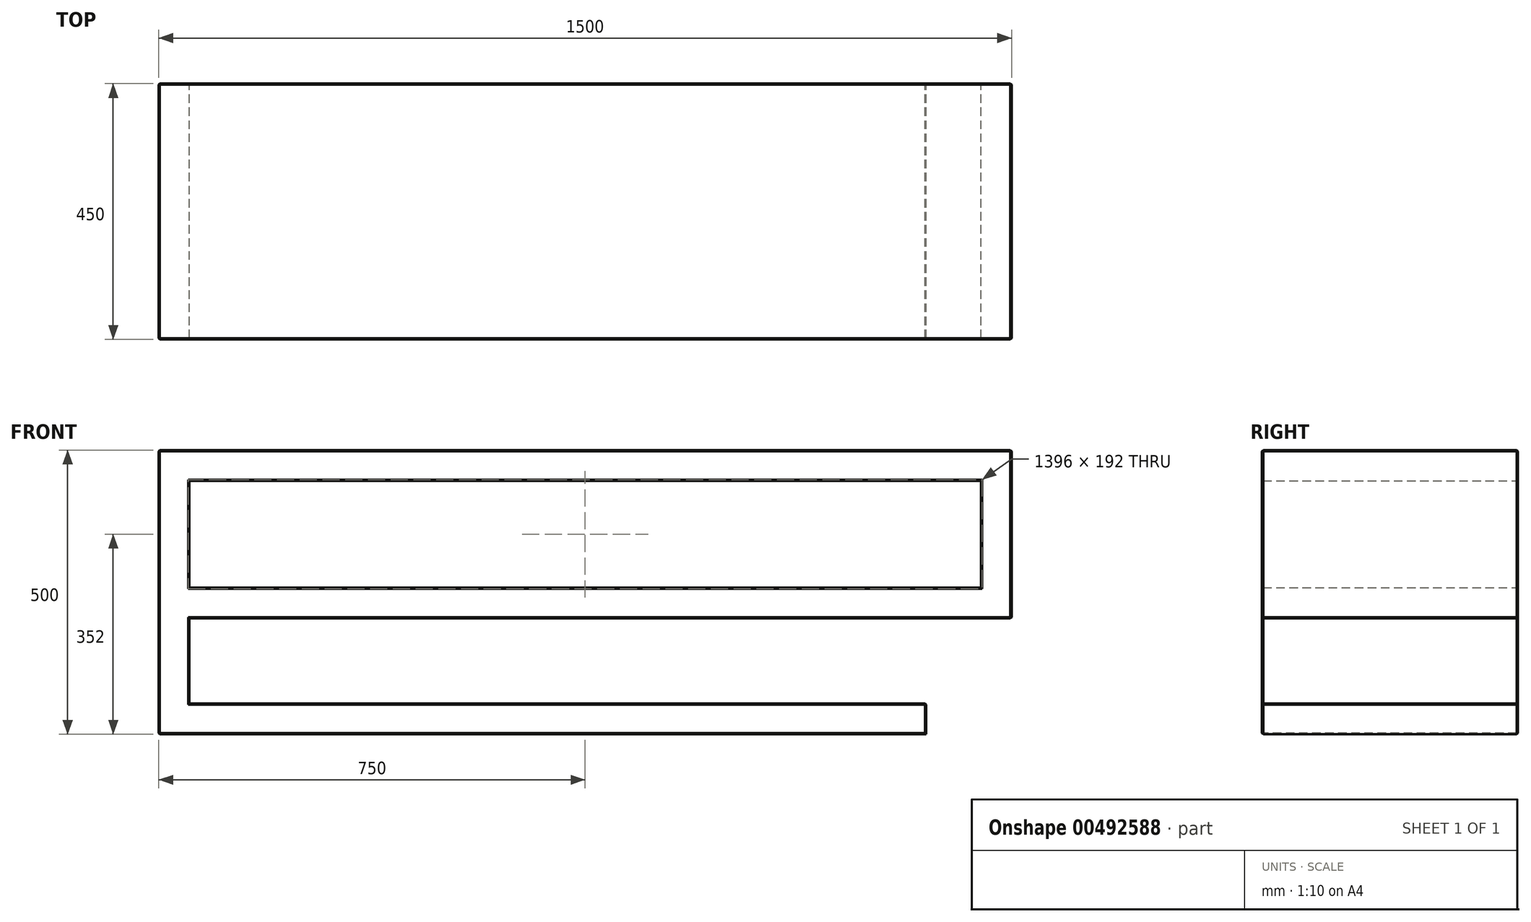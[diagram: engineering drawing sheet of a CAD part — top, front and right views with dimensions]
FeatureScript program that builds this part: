
annotation { "Feature Type Name" : "Feature", "Feature Type Description" : "" }
export const myFeature = defineFeature(function(context is Context, id is Id, definition is map)
    precondition{}
    {
        {
            var Q0;
            Q0=qCreatedBy(makeId("Front.planeOp"),FACE);
            var sketch = newSketch(context, id + "F0", { "sketchPlane" : qUnion([Q0])});
            skLineSegment(sketch, "E0.bottom", {"start": v(-750, 250) * mm, "end": v(750, 250) * mm});
            skLineSegment(sketch, "E0.left", {"start": v(-750, 250) * mm, "end": v(-750, -250) * mm});
            skLineSegment(sketch, "E0.right", {"start": v(750, 250) * mm, "end": v(750, -46) * mm});
            skPoint(sketch, "E0.middle", {"position": v(0, 0) * mm});
            skLineSegment(sketch, "E1", {"start": v(600, -196) * mm, "end": v(-696, -196) * mm});
            skLineSegment(sketch, "E2", {"start": v(-696, -196) * mm, "end": v(-696, -46) * mm});
            skLineSegment(sketch, "E3", {"start": v(-696, -46) * mm, "end": v(750, -46) * mm});
            skLineSegment(sketch, "E4.bottom", {"start": v(-696, 196) * mm, "end": v(696, 196) * mm});
            skLineSegment(sketch, "E4.top", {"start": v(-696, 8) * mm, "end": v(696, 8) * mm});
            skLineSegment(sketch, "E4.left", {"start": v(-696, 196) * mm, "end": v(-696, 8) * mm});
            skLineSegment(sketch, "E4.right", {"start": v(696, 196) * mm, "end": v(696, 8) * mm});
            skLineSegment(sketch, "E5", {"start": v(-750, -250) * mm, "end": v(600, -250) * mm});
            skLineSegment(sketch, "E6", {"start": v(600, -250) * mm, "end": v(600, -196) * mm});
            skSolve(sketch);
        }
        {
            var Q0;
            Q0=makeQuery(id+"F0.imprint","IMPRINT",FACE,{"disambiguationData":[TD([[makeQuery(id+"F0.imprint","IMPRINT",EDGE,{"derivedFrom":sQuery(id+"F0.wireOp",EDGE,"E0.bottom")}),-1.0]])]});
            extrude(context, id + "F1", {"entities" : qUnion([Q0]), "depth" : 450 * mm});
        }
        {
            var Q0;
            Q0=makeQuery(id+"F1.opExtrude","SWEPT_FACE",FACE,{"disambiguationData":[OSD([sQuery(id+"F0.wireOp",EDGE,"E0.left")])]});
            var Q1;
            Q1=makeQuery(id+"F1.opExtrude","SWEPT_FACE",FACE,{"disambiguationData":[OSD([sQuery(id+"F0.wireOp",EDGE,"E0.bottom")])]});
            var Q2;
            Q2=makeQuery(id+"F1.opExtrude","SWEPT_FACE",FACE,{"disambiguationData":[OSD([sQuery(id+"F0.wireOp",EDGE,"E0.right")])]});
            var Q3;
            Q3=makeQuery(id+"F1.opExtrude","SWEPT_FACE",FACE,{"disambiguationData":[OSD([sQuery(id+"F0.wireOp",EDGE,"4de1087b-30c0-4ecd-ada1-c2754f5ddcb1.trimOffspring")])]});
            var Q4;
            Q4=makeQuery(id+"F1.opExtrude","CAP_FACE",FACE,{"disambiguationData":[OSD([sQuery(id+"F0.wireOp",EDGE,"E0.bottom"),sQuery(id+"F0.wireOp",EDGE,"E0.top"),sQuery(id+"F0.wireOp",EDGE,"E0.left"),sQuery(id+"F0.wireOp",EDGE,"E0.right"),sQuery(id+"F0.wireOp",EDGE,"E1"),sQuery(id+"F0.wireOp",EDGE,"E2"),sQuery(id+"F0.wireOp",EDGE,"E3"),sQuery(id+"F0.wireOp",EDGE,"E4.bottom"),sQuery(id+"F0.wireOp",EDGE,"E4.top"),sQuery(id+"F0.wireOp",EDGE,"E4.left"),sQuery(id+"F0.wireOp",EDGE,"E4.right"),sQuery(id+"F0.wireOp",EDGE,"4de1087b-30c0-4ecd-ada1-c2754f5ddcb1.trimOffspring")])],"isStart":false});
            var Q5;
            Q5=makeQuery(id+"F1.opExtrude","CAP_FACE",FACE,{"disambiguationData":[OSD([sQuery(id+"F0.wireOp",EDGE,"E0.bottom"),sQuery(id+"F0.wireOp",EDGE,"E0.top"),sQuery(id+"F0.wireOp",EDGE,"E0.left"),sQuery(id+"F0.wireOp",EDGE,"E0.right"),sQuery(id+"F0.wireOp",EDGE,"E1"),sQuery(id+"F0.wireOp",EDGE,"E2"),sQuery(id+"F0.wireOp",EDGE,"E3"),sQuery(id+"F0.wireOp",EDGE,"E4.bottom"),sQuery(id+"F0.wireOp",EDGE,"E4.top"),sQuery(id+"F0.wireOp",EDGE,"E4.left"),sQuery(id+"F0.wireOp",EDGE,"E4.right"),sQuery(id+"F0.wireOp",EDGE,"4de1087b-30c0-4ecd-ada1-c2754f5ddcb1.trimOffspring")])],"isStart":true});
            var Q6;
            Q6=makeQuery(id+"F1.opExtrude","SWEPT_EDGE",EDGE,{"disambiguationData":[OSD([sQuery(id+"F0.wireOp",EDGE,"E1"),sQuery(id+"F0.wireOp",EDGE,"E6")])]});
            chamfer(context, id + "F2", {"entities" : qUnion([Q0, Q1, Q2, Q3, Q4, Q5, Q6]), "width" : 2 * mm, "tangentPropagation" : true});
        }
    });
